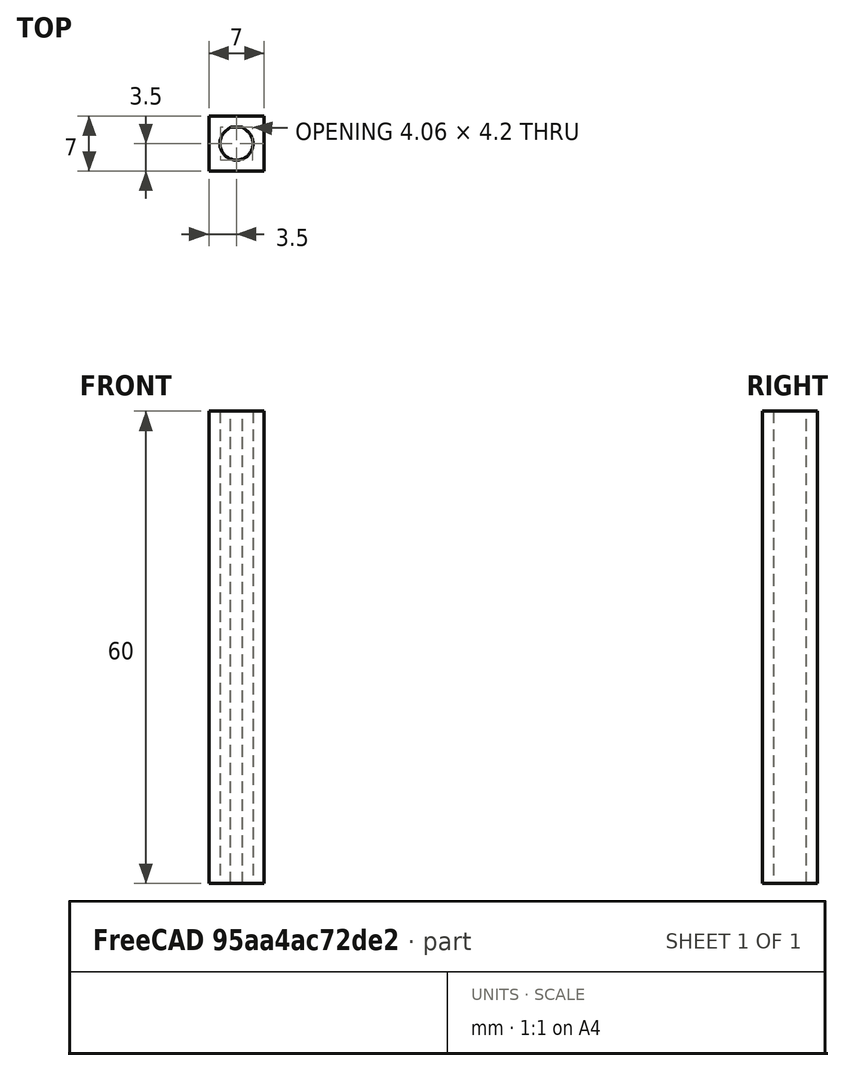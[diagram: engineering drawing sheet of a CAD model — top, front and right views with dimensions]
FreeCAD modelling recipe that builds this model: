
FCSTD DOCUMENT  (FreeCAD 0.19R24366 (Git))
Label: PTFETubeCutTool
License: Creative Commons Attribution-NonCommercial-ShareAlike
LicenseURL: http://creativecommons.org/licenses/by-nc-sa/4.0/
objects: Sketcher::SketchObject×1, PartDesign::Pad×1, PartDesign::Body×1
note: 4 computed .brp shape members not serialized (recipe doc carries the construction recipe); baked Part::Feature solids carry a one-line shape summary decoded from their .brp

FEATURE [Sketcher::SketchObject] Sketch
  FullyConstrained = false
  MapMode = 5
  Support = -> [XY_Plane]
  expr: Constraints[10] = .Constraints.D + 2.8mm
  sketch-geometry (13):
    g0: LineSegment StartX=-3.5 StartY=3.5 StartZ=0 EndX=3.5 EndY=3.5 EndZ=0
    g1: LineSegment StartX=3.5 StartY=3.5 StartZ=0 EndX=3.5 EndY=-3.5 EndZ=0
    g2: LineSegment StartX=3.5 StartY=-3.5 StartZ=0 EndX=-3.5 EndY=-3.5 EndZ=0
    g3: LineSegment StartX=-3.5 StartY=-3.5 StartZ=0 EndX=-3.5 EndY=3.5 EndZ=0
    g4: ArcOfCircle CenterX=0 CenterY=0 CenterZ=0 NormalX=0 NormalY=0 NormalZ=1 AngleXU=0 Radius=2.1 StartAngle=2.26893 EndAngle=7.15585
    g5: LineSegment StartX=-1.34985 StartY=1.60869 StartZ=0 EndX=1.34985 EndY=1.60869 EndZ=0
    g6: LineSegment StartX=-0.764337 StartY=2.1 StartZ=0 EndX=-2.1 EndY=2.1 EndZ=0
    g7: LineSegment StartX=-2.1 StartY=2.1 StartZ=0 EndX=-2.1 EndY=-2.1 EndZ=0
    g8: LineSegment StartX=-2.1 StartY=-2.1 StartZ=0 EndX=2.1 EndY=-2.1 EndZ=0
    g9: LineSegment StartX=2.1 StartY=-2.1 StartZ=0 EndX=2.1 EndY=2.1 EndZ=0
    g10: LineSegment StartX=-0.764337 StartY=2.1 StartZ=0 EndX=-1.34985 EndY=1.60869 EndZ=0
    g11: LineSegment StartX=-0.764337 StartY=2.1 StartZ=0 EndX=0.764337 EndY=2.1 EndZ=0
    g12: LineSegment StartX=0.764337 StartY=2.1 StartZ=0 EndX=1.34985 EndY=1.60869 EndZ=0
  constraints (33):
    c: Coincident(g0,g1)
    c: Coincident(g1,g2)
    c: Coincident(g2,g3)
    c: Coincident(g3,g0)
    c: Horizontal(g0)
    c: Horizontal(g2)
    c: Vertical(g1)
    c: Vertical(g3)
    c: Symmetric(g0,g1,g-1)
    c: Equal(g3,g0)
    c: DistanceX(g0,g0) = 7
    c: Coincident(g4,g-1)
    c: Coincident(g5,g4)
    c: Horizontal(g5)
    c: Coincident(g5,g4)
    c: Horizontal(g6)
    c: Coincident(g6,g7)
    c: Vertical(g7)
    c: Tangent(g7,g4)
    c: Coincident(g7,g8)
    c: Horizontal(g8)
    c: Tangent(g8,g4)
    c: Coincident(g8,g9)
    c: Vertical(g9)
    c: DistanceX(g8,g8) = 4.2  'D'
    c: Symmetric(g6,g8,g4)
    c: Tangent(g4,g10) = -1.5708
    c: Angle(g5,g10) = 0.698132
    c: Coincident(g6,g10)
    c: Coincident(g11,g10)
    c: Coincident(g12,g11)
    c: Symmetric(g10,g11,g-2)
    c: Coincident(g12,g4)
FEATURE [PartDesign::Pad] Pad
  Direction = (1,1,1)
  Length = 60
  Length2 = 100
  Profile = -> Sketch
  Type = 0
FEATURE [PartDesign::Body] Body
  Group = -> [Sketch,Pad]
  Origin = -> Origin
  Tip = -> Pad
